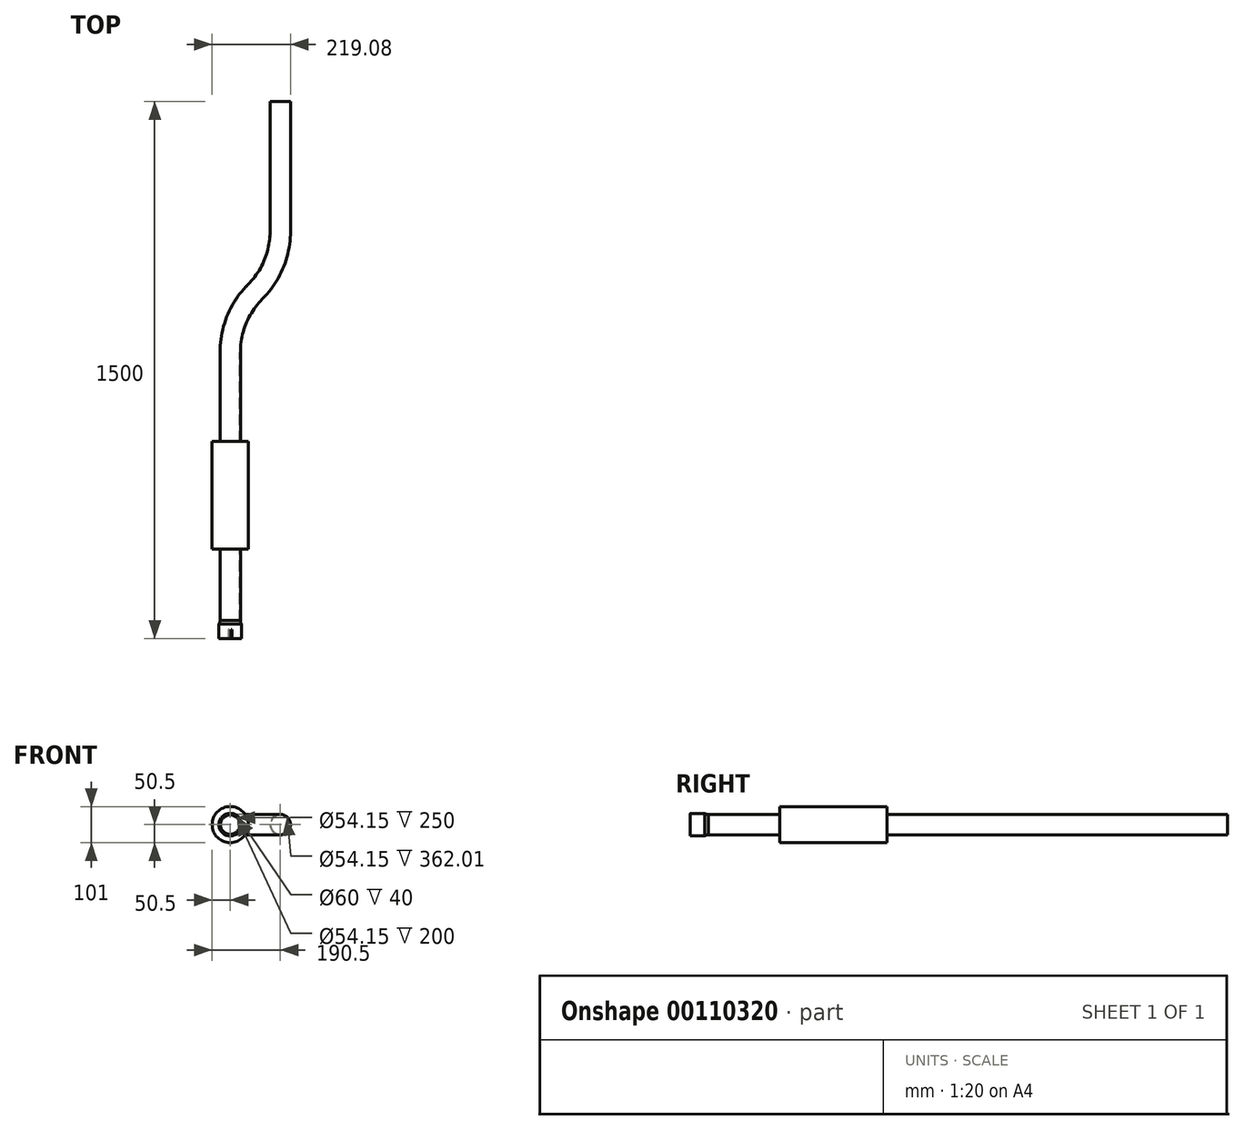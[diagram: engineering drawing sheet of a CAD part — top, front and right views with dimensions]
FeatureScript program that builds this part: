
annotation { "Feature Type Name" : "Feature", "Feature Type Description" : "" }
export const myFeature = defineFeature(function(context is Context, id is Id, definition is map)
    precondition{}
    {
        {
            var Q0;
            Q0=qCreatedBy(makeId("Front.planeOp"),FACE);
            var sketch = newSketch(context, id + "F0", { "sketchPlane" : qUnion([Q0])});
            skCircle(sketch, "E0", {"center": v(0, 0) * mm, "radius": 28.57 * mm});
            skCircle(sketch, "E1.0", {"center": v(0, 0) * mm, "radius": 27.07 * mm});
            skSolve(sketch);
        }
        {
            var Q0;
            Q0=qCreatedBy(makeId("Top.planeOp"),FACE);
            var sketch = newSketch(context, id + "F1", { "sketchPlane" : qUnion([Q0])});
            skLineSegment(sketch, "E2", {"start": v(0, 0) * mm, "end": v(0, 750) * mm});
            skLineSegment(sketch, "E3", {"start": v(70, 919) * mm, "end": v(70, 919) * mm});
            skLineSegment(sketch, "E4", {"start": v(140, 1087.99) * mm, "end": v(140, 1450) * mm});
            skPoint(sketch, "E5.visualSharp", {"position": v(0, 849) * mm});
            skArc(sketch, "E5.filletArc", {"start": v(70, 919) * mm, "mid": v(18.2, 841.46) * mm, "end": v(0, 750) * mm});
            skPoint(sketch, "E6.visualSharp", {"position": v(140, 989) * mm});
            skArc(sketch, "E6.filletArc", {"start": v(70, 919) * mm, "mid": v(121.8, 996.53) * mm, "end": v(140, 1087.99) * mm});
            skSolve(sketch);
        }
        {
            var Q0;
            Q0=makeQuery(id+"F0.imprint","IMPRINT",FACE,{"disambiguationData":[TD([[makeQuery(id+"F0.imprint","IMPRINT",EDGE,{"derivedFrom":sQuery(id+"F0.wireOp",EDGE,"E0")}),1.0]])]});
            var Q1;
            Q1=sQuery(id+"F1.wireOp",EDGE,"E2");
            var Q2;
            Q2=sQuery(id+"F1.wireOp",EDGE,"E5.filletArc");
            var Q3;
            Q3=sQuery(id+"F1.wireOp",EDGE,"E3");
            var Q4;
            Q4=sQuery(id+"F1.wireOp",EDGE,"E6.filletArc");
            var Q5;
            Q5=sQuery(id+"F1.wireOp",EDGE,"E4");
            sweep(context, id + "F2", {"profiles" : qUnion([Q0]), "path" : qUnion([Q1, Q2, Q3, Q4, Q5])});
        }
        {
            var Q0;
            Q0=qCreatedBy(makeId("Right.planeOp"),FACE);
            var sketch = newSketch(context, id + "F3", { "sketchPlane" : qUnion([Q0])});
            skLineSegment(sketch, "E7.bottom", {"start": v(-50, 30) * mm, "end": v(-10, 30) * mm});
            skLineSegment(sketch, "E7.left", {"start": v(-50, 30) * mm, "end": v(-50, 31.5) * mm});
            skLineSegment(sketch, "E8.0", {"start": v(0, -27.07) * mm, "end": v(0, 27.07) * mm});
            skLineSegment(sketch, "E8.1", {"start": v(0, 28.57) * mm, "end": v(0, -28.57) * mm});
            skFitSpline(sketch, "E9", {"points": [v(0, 27.07) * mm, v(-10, 30) * mm], "startDerivative": vector(-25.5, 0) * mm, "endDerivative": vector(-4.5, 0) * mm});
            skLineSegment(sketch, "E10", {"start": v(0, 0) * mm, "end": v(-109.15, 0) * mm, "construction": true});
            skLineSegment(sketch, "E11", {"start": v(-10, 30) * mm, "end": v(-10, 31.5) * mm});
            skLineSegment(sketch, "E12", {"start": v(-50, 31.5) * mm, "end": v(-10, 31.5) * mm});
            skFitSpline(sketch, "E13", {"points": [v(-10, 31.5) * mm, v(0, 28.57) * mm], "startDerivative": vector(4.5, 0) * mm, "endDerivative": vector(25.5, 0) * mm});
            skSolve(sketch);
        }
        {
            var Q0;
            Q0 = qSketchRegion(id + "F3", true);
            var Q1;
            Q1=sQuery(id+"F3.wireOp",EDGE,"E10");
            revolve(context, id + "F4", {"operationType" : NewBodyOperationType.ADD, "entities" : qUnion([Q0]), "axis" : qUnion([Q1]), "revolveType" : RevolveType.FULL});
        }
        {
            var Q0;
            Q0=makeQuery(id+"F4.opRevolve","SWEPT_FACE",FACE,{"disambiguationData":[OSD([sQuery(id+"F3.wireOp",EDGE,"E7.left")])]});
            var sketch = newSketch(context, id + "F5", { "sketchPlane" : qUnion([Q0])});
            skCircle(sketch, "E14.0", {"center": v(0, 0) * mm, "radius": 30 * mm, "construction": true});
            skCircle(sketch, "E15.0", {"center": v(0, 0) * mm, "radius": 31.5 * mm, "construction": true});
            skLineSegment(sketch, "E16", {"start": v(2.75, 31.38) * mm, "end": v(2.61, 29.89) * mm});
            skLineSegment(sketch, "E17", {"start": v(0, 0) * mm, "end": v(0, 42.79) * mm, "construction": true});
            skLineSegment(sketch, "E18", {"start": v(0, 0) * mm, "end": v(1.98, 22.66) * mm, "construction": true});
            skLineSegment(sketch, "E19", {"start": v(5.23, 31.06) * mm, "end": v(4.98, 29.58) * mm});
            skLineSegment(sketch, "E20.1.0", {"start": v(-2.75, -31.38) * mm, "end": v(-2.61, -29.89) * mm});
            skLineSegment(sketch, "E20.1.1", {"start": v(-5.23, -31.06) * mm, "end": v(-4.98, -29.58) * mm});
            skLineSegment(sketch, "E20.anchor1", {"start": v(0, 0) * mm, "end": v(2.61, 29.89) * mm, "construction": true});
            skLineSegment(sketch, "E20.anchor2", {"start": v(0, 0) * mm, "end": v(-2.61, -29.89) * mm, "construction": true});
            skSolve(sketch);
        }
        {
            var Q0;
            {var subQ0=sQuery(id+"F5.wireOp",EDGE,"E20.2.0");Q0=makeQuery(id+"F5.imprint","IMPRINT",FACE,{"disambiguationData":[TD([[makeQuery(id+"F5.imprint","IMPRINT",EDGE,{"derivedFrom":subQ0}),1.0]])]});}
            var Q1;
            {var subQ0=sQuery(id+"F5.wireOp",EDGE,"E16");Q1=makeQuery(id+"F5.imprint","IMPRINT",FACE,{"disambiguationData":[TD([[makeQuery(id+"F5.imprint","IMPRINT",EDGE,{"derivedFrom":subQ0}),1.0]])]});}
            var Q2;
            {var subQ0=sQuery(id+"F5.wireOp",EDGE,"E20.1.0");Q2=makeQuery(id+"F5.imprint","IMPRINT",FACE,{"disambiguationData":[TD([[makeQuery(id+"F5.imprint","IMPRINT",EDGE,{"derivedFrom":subQ0}),1.0]])]});}
            extrude(context, id + "F6", {"entities" : qUnion([Q0, Q1, Q2]), "operationType" : NewBodyOperationType.REMOVE, "oppositeDirection" : true, "depth" : 25 * mm});
        }
        {
            var Q0;
            Q0=qCreatedBy(makeId("Front.planeOp"),FACE);
            cPlane(context, id + "F7", {"entities" : qUnion([Q0]), "cplaneType" : CPlaneType.OFFSET, "offset" : 200 * mm, "oppositeDirection" : true, "width" : 150 * mm, "height" : 150 * mm});
        }
        {
            var Q0;
            Q0=qCreatedBy(id+"F7.planeOp",FACE);
            var sketch = newSketch(context, id + "F8", { "sketchPlane" : qUnion([Q0])});
            skCircle(sketch, "E21", {"center": v(0, 0) * mm, "radius": 50.5 * mm});
            skSolve(sketch);
        }
        {
            var Q0;
            Q0=makeQuery(id+"F8.imprint","IMPRINT",FACE,{"disambiguationData":[TD([[makeQuery(id+"F8.imprint","IMPRINT",EDGE,{"derivedFrom":sQuery(id+"F8.wireOp",EDGE,"E21")}),1.0]])]});
            extrude(context, id + "F9", {"entities" : qUnion([Q0]), "operationType" : NewBodyOperationType.ADD, "oppositeDirection" : true, "depth" : 300 * mm, "offsetDistance" : 25 * mm});
        }
    });
